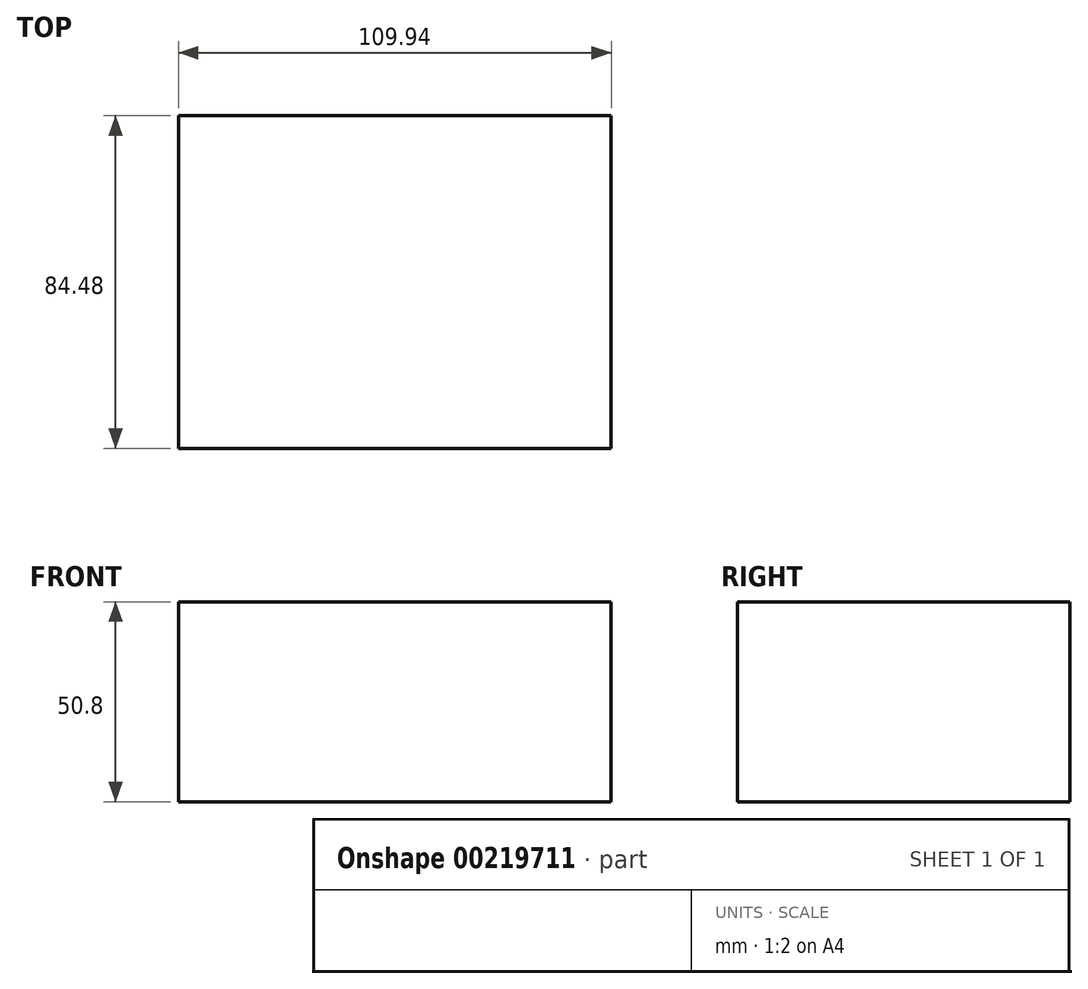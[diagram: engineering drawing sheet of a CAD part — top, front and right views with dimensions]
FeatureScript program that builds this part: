
annotation { "Feature Type Name" : "Feature", "Feature Type Description" : "" }
export const myFeature = defineFeature(function(context is Context, id is Id, definition is map)
    precondition{}
    {
        {
            var Q0;
            Q0=qCreatedBy(makeId("Top.planeOp"),FACE);
            var sketch = newSketch(context, id + "F0", { "sketchPlane" : qUnion([Q0])});
            skLineSegment(sketch, "E0.bottom", {"start": v(-54.97, 42.24) * mm, "end": v(54.97, 42.24) * mm});
            skLineSegment(sketch, "E0.top", {"start": v(-54.97, -42.24) * mm, "end": v(54.97, -42.24) * mm});
            skLineSegment(sketch, "E0.left", {"start": v(-54.97, 42.24) * mm, "end": v(-54.97, -42.24) * mm});
            skLineSegment(sketch, "E0.right", {"start": v(54.97, 42.24) * mm, "end": v(54.97, -42.24) * mm});
            skPoint(sketch, "E0.middle", {"position": v(0, 0) * mm});
            skSolve(sketch);
        }
        {
            var Q0;
            Q0=makeQuery(id+"F0.imprint","IMPRINT",FACE,{"disambiguationData":[TD([[makeQuery(id+"F0.imprint","IMPRINT",EDGE,{"derivedFrom":sQuery(id+"F0.wireOp",EDGE,"E0.bottom")}),-1.0]])]});
            extrude(context, id + "F1", {"entities" : qUnion([Q0]), "depth" : 50.8 * mm});
        }
    });
